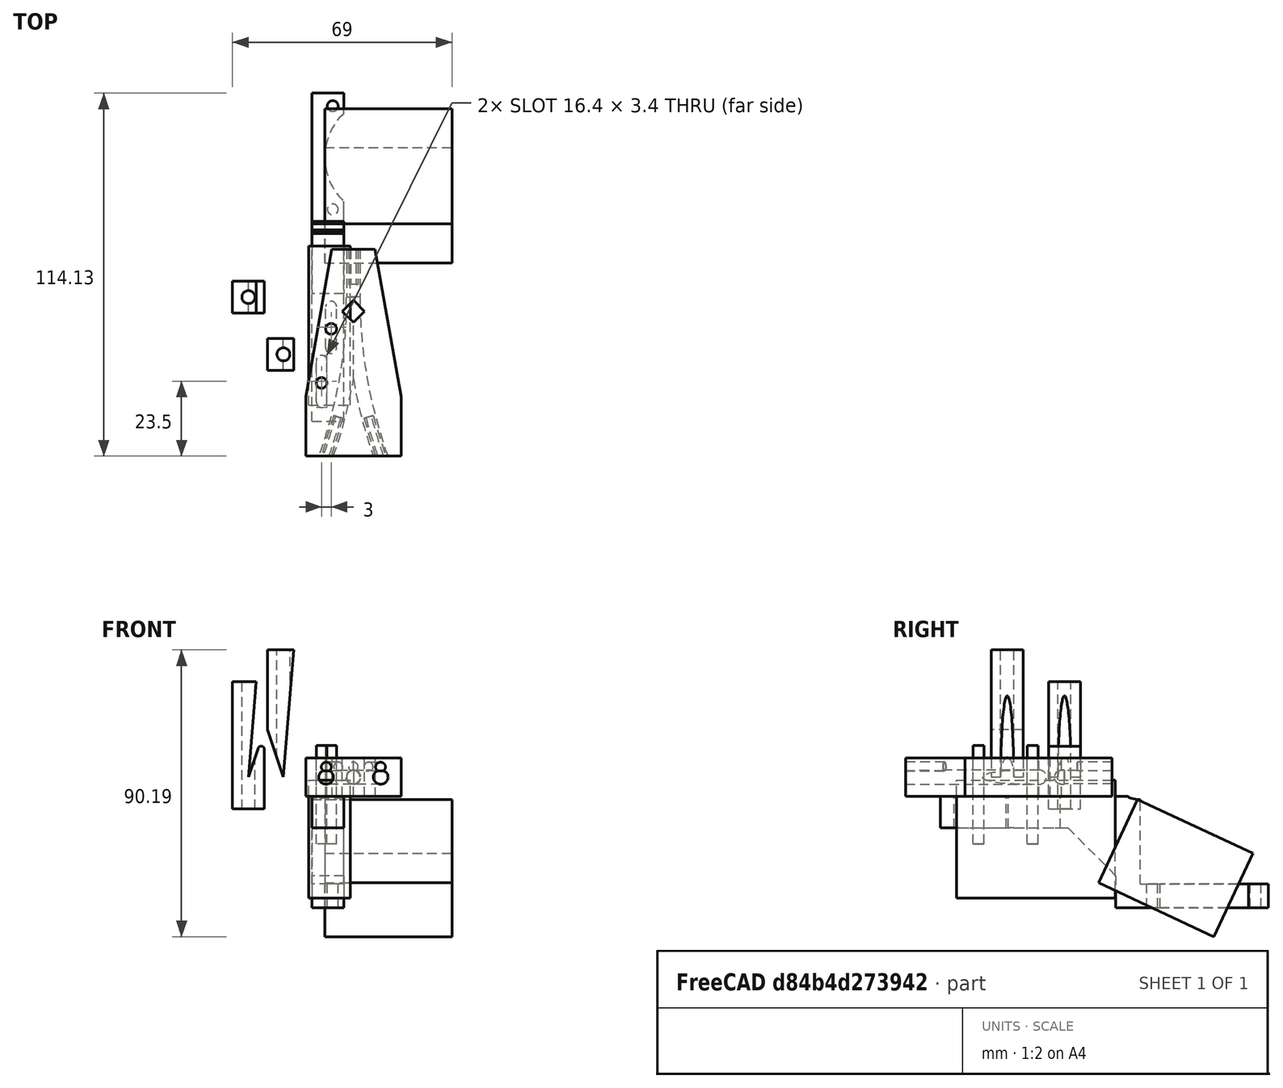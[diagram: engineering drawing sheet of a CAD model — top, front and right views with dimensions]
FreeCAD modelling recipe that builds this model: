
FCSTD DOCUMENT  (FreeCAD 0.16R6703 (Git))
Label: ptfe traintracks
License: All rights reserved
LicenseURL: http://en.wikipedia.org/wiki/All_rights_reserved
objects: Part::Cut×23, Part::Box×18, Part::Cylinder×15, Part::Fuse×6, Part::Chamfer×4, Part::Torus×2, Part::Fillet×1, Part::Mirroring×1
note: 70 computed .brp shape members not serialized (recipe doc carries the construction recipe); baked Part::Feature solids carry a one-line shape summary decoded from their .brp

FEATURE [Part::Torus] Torus
  Angle1 = -180
  Angle2 = 180
  Angle3 = 360
  Placement = pos=(-150,0,0) rot=(0,0,1;0rad)
  Radius1 = 10
  Radius2 = 2
FEATURE [Part::Torus] Torus001
  Angle1 = -180
  Angle2 = 180
  Angle3 = 360
  Placement = pos=(150,0,0) rot=(0,0,1;0rad)
  Radius1 = 10
  Radius2 = 2
FEATURE [Part::Box] Box  label="Cube"
  Height = 10
  Length = 700
  Placement = pos=(-350,0,-4) rot=(0,0,1;0rad)
  Width = 300
FEATURE [Part::Box] Box001  label="Cube001"
  Height = 10
  Length = 700
  Placement = pos=(-350,0,-4) rot=(0,0,1;0rad)
  Width = 300
FEATURE [Part::Cut] Cut
  Base = -> Torus001
  Tool = -> Box001
FEATURE [Part::Cut] Cut001
  Base = -> Torus
  Tool = -> Box
FEATURE [Part::Cylinder] Cylinder
  Angle = 360
  Height = 20
  Placement = pos=(0,20,0) rot=(1,0,0;1.5708rad)
  Radius = 2.1
FEATURE [Part::Box] Box002  label="Cube002"
  Height = 12
  Length = 30
  Placement = pos=(-15,-50,-6) rot=(0,0,1;0rad)
  Width = 65
FEATURE [Part::Cylinder] Cylinder001  label="grub"
  Angle = 360
  Height = 16
  Placement = pos=(4.76732,-37.7222,3.2) rot=(0.978386,0.146221,0.146221;1.59265rad)
  Radius = 1.5
FEATURE [Part::Cut] Cut002
  Base = -> Box002
  Tool = -> Cut
FEATURE [Part::Cut] Cut003
  Base = -> Cut002
  Tool = -> Cut001
FEATURE [Part::Cut] Cut004
  Base = -> Cut003
  Tool = -> Cylinder
FEATURE [Part::Cylinder] Cylinder005  label="grub001"
  Angle = 360
  Height = 17
  Placement = pos=(-4.76732,-37.7222,3.2) rot=(0.978386,-0.146221,-0.146221;1.59265rad)
  Radius = 1.5
FEATURE [Part::Cylinder] Cylinder006  label="grub002"
  Angle = 360
  Height = 13
  Placement = pos=(0,17,3.2) rot=(1,0,0;1.5708rad)
  Radius = 1.5
FEATURE [Part::Cut] Cut005
  Base = -> Cut004
  Tool = -> Cylinder005
FEATURE [Part::Cut] Cut006
  Base = -> Cut005
  Tool = -> Cylinder001
FEATURE [Part::Cut] Cut007
  Base = -> Cut006
  Tool = -> Cylinder006
FEATURE [Part::Box] Box003  label="Cube003"
  Height = 17
  Length = 5
  Placement = pos=(0,-8,-9) rot=(0,0,1;0.785398rad)
  Width = 5
FEATURE [Part::Cut] Cut008
  Base = -> Cut007
  Tool = -> Box003
FEATURE [Part::Box] Box004  label="Cube004"
  Height = 18
  Length = 24
  Placement = pos=(16,-37,-9) rot=(0,0,1;0.174533rad)
  Width = 60
FEATURE [Part::Box] Box005  label="Cube005"
  Height = 18
  Length = 24
  Placement = pos=(-39.6354,-32.8324,-9) rot=(0,0,-1;0.174533rad)
  Width = 60
FEATURE [Part::Cut] Cut009
  Base = -> Cut008
  Tool = -> Box004
FEATURE [Part::Cut] Cut010  label="y-blocka"
  Base = -> Cut009
  Tool = -> Box005
FEATURE [Part::Cylinder] Cylinder007  label="Cylinder001"
  Angle = 360
  Height = 100
  Placement = pos=(0,0,-27) rot=(0,0,1;0rad)
  Radius = 2.05
FEATURE [Part::Box] Box006  label="Cube006"
  Height = 40
  Length = 10
  Placement = pos=(-5,-5,-10) rot=(0,0,1;0rad)
  Width = 10
FEATURE [Part::Box] Box007  label="Cube007"
  Height = 33
  Length = 10
  Placement = pos=(0,-11,0) rot=(0,1,0;0.324177rad)
  Width = 22
FEATURE [Part::Box] Box008  label="Cube008"
  Height = 33
  Length = 10
  Placement = pos=(0,-11,0) rot=(0,1,0;0.079831rad)
  Width = 22
FEATURE [Part::Cut] Cut011
  Base = -> Box008
  Tool = -> Box007
FEATURE [Part::Cut] Cut012
  Base = -> Box006
  Tool = -> Cut011
FEATURE [Part::Fillet] Fillet
  Base = -> Cut012
  Edges = 1 edges r=1: [Edge17]
FEATURE [Part::Cut] Cut013  label="tube-cut-1"
  Base = -> Fillet
  Placement = pos=(-33,0,0) rot=(0,0,1;0rad)
  Tool = -> Cylinder007
FEATURE [Part::Box] Box009  label="Cube009"
  Height = 33
  Length = 10
  Placement = pos=(0,-11,0) rot=(0,1,0;0.324177rad)
  Width = 22
FEATURE [Part::Box] Box010  label="Cube010"
  Height = 45
  Length = 10
  Placement = pos=(0,-11,0) rot=(0,1,0;0.079831rad)
  Width = 22
FEATURE [Part::Cylinder] Cylinder008  label="Cylinder002"
  Angle = 360
  Height = 100
  Placement = pos=(0,0,-27) rot=(0,0,1;0rad)
  Radius = 2.05
FEATURE [Part::Mirroring] Part__Mirroring  label="Cube009 (Mirror #1)"
  Base = (0,0,0)
  Normal = (1,0,0)
  Source = -> Box009
FEATURE [Part::Box] Box011  label="Cube011"
  Height = 40
  Length = 10
  Placement = pos=(-5,-5,0) rot=(0,0,1;0rad)
  Width = 10
FEATURE [Part::Cut] Cut014
  Base = -> Box011
  Tool = -> Box010
FEATURE [Part::Cut] Cut015
  Base = -> Cut014
  Tool = -> Part__Mirroring
FEATURE [Part::Cut] Cut016  label="tube-cut-2"
  Base = -> Cut015
  Placement = pos=(-22,-18,0) rot=(0,0,1;0rad)
  Tool = -> Cylinder008
FEATURE [Part::Cylinder] Cylinder009  label="Cylinder003"
  Angle = 360
  Height = 31
  Placement = pos=(-10,-27,-21) rot=(0,0,1;0rad)
  Radius = 1.7
FEATURE [Part::Cylinder] Cylinder010  label="Cylinder004"
  Angle = 360
  Height = 31
  Placement = pos=(-7,-10,-21) rot=(0,0,1;0rad)
  Radius = 1.7
FEATURE [Part::Cut] Cut017
  Base = -> Cut010
  Tool = -> Cylinder009
FEATURE [Part::Cut] Cut018  label="y-block"
  Base = -> Cut017
  Tool = -> Cylinder010
FEATURE [Part::Box] Box013  label="Cube013"
  Height = 48
  Length = 10
  Placement = pos=(0,15,-6) rot=(-1,0,0;2.00713rad)
  Width = 34
FEATURE [Part::Box] Box014  label="fan-heatsink"
  Height = 40
  Length = 40
  Placement = pos=(-9,23,-7) rot=(-1,0,0;2.00713rad)
  Width = 29
FEATURE [Part::Cylinder] Cylinder013  label="Cylinder018"
  Angle = 360
  Height = 31
  Placement = pos=(10,-27,-21) rot=(0,0,1;0rad)
  Radius = 1.7
FEATURE [Part::Cylinder] Cylinder014  label="Cylinder019"
  Angle = 360
  Height = 31
  Placement = pos=(10,-59.5,-21) rot=(0,0,1;0rad)
  Radius = 1.7
FEATURE [Part::Fuse] Fusion
  Base = -> Cylinder013
  Placement = pos=(-7.5,70,-56) rot=(-1,0,0;0.436332rad)
  Tool = -> Cylinder014
FEATURE [Part::Cylinder] Cylinder015  label="Cylinder020"
  Angle = 360
  Height = 31
  Placement = pos=(-10,-27,-21) rot=(0,0,1;0rad)
  Radius = 1.7
FEATURE [Part::Cylinder] Cylinder016  label="Cylinder021"
  Angle = 360
  Height = 31
  Placement = pos=(-7,-10,-21) rot=(0,0,1;0rad)
  Radius = 1.7
FEATURE [Part::Cylinder] Cylinder017  label="Cylinder022"
  Angle = 360
  Height = 22
  Placement = pos=(19,21,-59) rot=(-1,0,0;0.436332rad)
  Radius = 19
FEATURE [Part::Box] Box015  label="Cube015"
  Height = 44
  Length = 55
  Placement = pos=(-24,23,-7) rot=(-1,0,0;2.00713rad)
  Width = 29
FEATURE [Part::Box] Box016  label="Cube016"
  Height = 37
  Length = 13
  Placement = pos=(-14,-34,-38) rot=(0,0,1;0rad)
  Width = 50
FEATURE [Part::Box] Box017  label="Cube017"
  Height = 10
  Length = 10
  Placement = pos=(-13,-39,-16) rot=(0,0,1;0rad)
  Width = 59
FEATURE [Part::Cylinder] Cylinder019  label="Cylinder026"
  Angle = 360
  Height = 31
  Placement = pos=(-10,-20,-21) rot=(0,0,1;0rad)
  Radius = 1.7
FEATURE [Part::Box] Box018  label="Cube018"
  Height = 15
  Length = 3.4
  Placement = pos=(-11.7,-33,-19) rot=(0,0,1;0rad)
  Width = 13
FEATURE [Part::Cylinder] Cylinder020  label="Cylinder027"
  Angle = 360
  Height = 31
  Placement = pos=(-10,-33,-21) rot=(0,0,1;0rad)
  Radius = 1.7
FEATURE [Part::Fuse] Fusion002
  Base = -> Box018
  Tool = -> Cylinder020
FEATURE [Part::Fuse] Fusion003  label="slot"
  Base = -> Cylinder019
  Tool = -> Fusion002
FEATURE [Part::Fuse] Fusion004  label="slot001"
  Base = -> Cylinder019
  Placement = pos=(3,17,0) rot=(0,0,1;0rad)
  Tool = -> Fusion002
FEATURE [Part::Cut] Cut019
  Base = -> Box013
  Placement = pos=(-13,0,0) rot=(0,0,1;0rad)
  Tool = -> Box015
FEATURE [Part::Fuse] Fusion005
  Base = -> Fusion
  Placement = pos=(-9,0,0) rot=(0,0,1;0rad)
  Tool = -> Cylinder017
FEATURE [Part::Cut] Cut020
  Base = -> Cut019
  Placement = pos=(0,0,-8) rot=(1,0,0;0.436332rad)
  Tool = -> Fusion005
FEATURE [Part::Fuse] Fusion006
  Base = -> Box017
  Tool = -> Cut020
FEATURE [Part::Cut] Cut021
  Base = -> Fusion006
  Tool = -> Fusion003
FEATURE [Part::Cut] Cut022
  Base = -> Cut021
  Tool = -> Fusion004
FEATURE [Part::Chamfer] Chamfer
  Base = -> Cut022
  Edges = 1 edges r=1: [Edge19]
FEATURE [Part::Chamfer] Chamfer001
  Base = -> Chamfer
  Edges = 1 edges r=1: [Edge46]
FEATURE [Part::Chamfer] Chamfer002
  Base = -> Chamfer001
  Edges = 1 edges r=1: [Edge13]
FEATURE [Part::Chamfer] Chamfer003  label="bracket"
  Base = -> Chamfer002
  Edges = 1 edges r=15: [Edge45]
